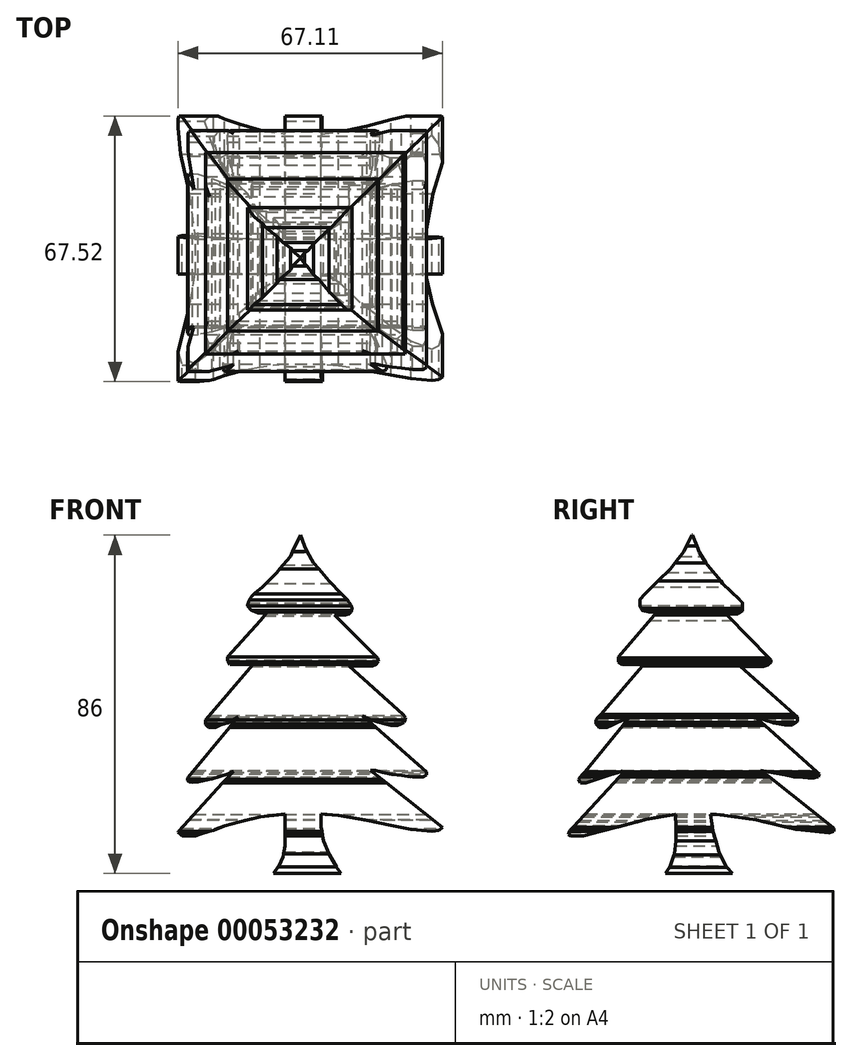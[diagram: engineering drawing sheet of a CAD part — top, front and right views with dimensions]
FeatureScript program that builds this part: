
annotation { "Feature Type Name" : "Feature", "Feature Type Description" : "" }
export const myFeature = defineFeature(function(context is Context, id is Id, definition is map)
    precondition{}
    {
        {
            var Q0;
            Q0=qCreatedBy(makeId("Front.planeOp"),FACE);
            var sketch = newSketch(context, id + "F0", { "sketchPlane" : qUnion([Q0])});
            skLineSegment(sketch, "E0", {"start": v(0, 37.34) * mm, "end": v(-2.57, 31.9) * mm});
            skLineSegment(sketch, "E1", {"start": v(-2.57, 31.9) * mm, "end": v(-6, 27.88) * mm});
            skLineSegment(sketch, "E2", {"start": v(-6, 27.88) * mm, "end": v(-9.62, 24.16) * mm});
            skLineSegment(sketch, "E3", {"start": v(-9.62, 24.16) * mm, "end": v(-13.44, 21.04) * mm});
            skLineSegment(sketch, "E4", {"start": v(-13.44, 21.04) * mm, "end": v(-13.44, 19.43) * mm});
            skLineSegment(sketch, "E5", {"start": v(-13.44, 19.43) * mm, "end": v(-12.53, 18.32) * mm});
            skLineSegment(sketch, "E6", {"start": v(-12.53, 18.32) * mm, "end": v(-10.82, 17.52) * mm});
            skLineSegment(sketch, "E7", {"start": v(-10.82, 17.52) * mm, "end": v(-8.61, 17.52) * mm});
            skLineSegment(sketch, "E8", {"start": v(-8.61, 17.52) * mm, "end": v(-10.12, 15.6) * mm});
            skLineSegment(sketch, "E9", {"start": v(-10.12, 15.6) * mm, "end": v(-18.47, 6.45) * mm});
            skLineSegment(sketch, "E10", {"start": v(-18.47, 6.45) * mm, "end": v(-18.47, 5.32) * mm});
            skLineSegment(sketch, "E11", {"start": v(-18.47, 5.32) * mm, "end": v(-17.83, 4.51) * mm});
            skLineSegment(sketch, "E12", {"start": v(-17.83, 4.51) * mm, "end": v(-16.4, 4.51) * mm});
            skLineSegment(sketch, "E13", {"start": v(-16.4, 4.51) * mm, "end": v(-14.4, 4.51) * mm});
            skLineSegment(sketch, "E14", {"start": v(-14.4, 4.51) * mm, "end": v(-12.08, 4.51) * mm});
            skLineSegment(sketch, "E15", {"start": v(-12.08, 4.51) * mm, "end": v(-24.1, -9.58) * mm});
            skLineSegment(sketch, "E16", {"start": v(-24.1, -9.58) * mm, "end": v(-24.1, -10.69) * mm});
            skLineSegment(sketch, "E17", {"start": v(-24.1, -10.69) * mm, "end": v(-23.3, -11.5) * mm});
            skLineSegment(sketch, "E18", {"start": v(-23.3, -11.5) * mm, "end": v(-21.58, -11.5) * mm});
            skLineSegment(sketch, "E19", {"start": v(-21.58, -11.5) * mm, "end": v(-20.27, -10.92) * mm});
            skLineSegment(sketch, "E20", {"start": v(-20.27, -10.92) * mm, "end": v(-18.56, -10.32) * mm});
            skLineSegment(sketch, "E21", {"start": v(-18.56, -10.32) * mm, "end": v(-15.85, -8.81) * mm});
            skLineSegment(sketch, "E22", {"start": v(-15.85, -8.81) * mm, "end": v(-28.5, -24.2) * mm});
            skLineSegment(sketch, "E23", {"start": v(-22.4, -24.55) * mm, "end": v(-20.48, -23.91) * mm});
            skLineSegment(sketch, "E24", {"start": v(-20.48, -23.91) * mm, "end": v(-18.4, -23.27) * mm});
            skLineSegment(sketch, "E25", {"start": v(-18.4, -23.27) * mm, "end": v(-17.05, -22.63) * mm});
            skLineSegment(sketch, "E26", {"start": v(-17.05, -22.63) * mm, "end": v(-31.07, -38.15) * mm});
            skLineSegment(sketch, "E27", {"start": v(-31.07, -38.15) * mm, "end": v(-30.1, -39.02) * mm});
            skLineSegment(sketch, "E28", {"start": v(-30.1, -39.02) * mm, "end": v(-26.6, -39.02) * mm});
            skLineSegment(sketch, "E29", {"start": v(-26.6, -39.02) * mm, "end": v(-22.1, -37.61) * mm});
            skLineSegment(sketch, "E30", {"start": v(-22.1, -37.61) * mm, "end": v(-19.29, -36.5) * mm});
            skLineSegment(sketch, "E31", {"start": v(-19.29, -36.5) * mm, "end": v(-15.46, -35.5) * mm});
            skLineSegment(sketch, "E32", {"start": v(-15.46, -35.5) * mm, "end": v(-10.23, -34.3) * mm});
            skLineSegment(sketch, "E33", {"start": v(-10.23, -34.3) * mm, "end": v(-2.99, -33.39) * mm});
            skLineSegment(sketch, "E34", {"start": v(-2.99, -33.39) * mm, "end": v(4.36, -33.39) * mm});
            skLineSegment(sketch, "E35", {"start": v(4.36, -33.39) * mm, "end": v(9.69, -33.9) * mm});
            skLineSegment(sketch, "E36", {"start": v(9.69, -33.9) * mm, "end": v(16.95, -35.14) * mm});
            skLineSegment(sketch, "E37", {"start": v(16.95, -35.14) * mm, "end": v(22.98, -36.42) * mm});
            skLineSegment(sketch, "E38", {"start": v(22.98, -36.42) * mm, "end": v(28.05, -37.4) * mm});
            skLineSegment(sketch, "E39", {"start": v(28.05, -37.4) * mm, "end": v(33.37, -37.96) * mm});
            skLineSegment(sketch, "E40", {"start": v(33.37, -37.96) * mm, "end": v(35.23, -37.7) * mm});
            skLineSegment(sketch, "E41", {"start": v(35.23, -37.7) * mm, "end": v(36.04, -36.93) * mm});
            skLineSegment(sketch, "E42", {"start": v(36.04, -36.93) * mm, "end": v(17.8, -22.45) * mm});
            skLineSegment(sketch, "E43", {"start": v(17.8, -22.45) * mm, "end": v(19.05, -22.45) * mm});
            skLineSegment(sketch, "E44", {"start": v(25.64, -23.69) * mm, "end": v(28.4, -24.14) * mm});
            skLineSegment(sketch, "E45", {"start": v(28.4, -24.14) * mm, "end": v(31.12, -24.14) * mm});
            skLineSegment(sketch, "E46", {"start": v(31.12, -24.14) * mm, "end": v(32.03, -23.64) * mm});
            skLineSegment(sketch, "E47", {"start": v(32.03, -23.64) * mm, "end": v(32.03, -22.78) * mm});
            skLineSegment(sketch, "E48", {"start": v(32.03, -22.78) * mm, "end": v(15.82, -8.6) * mm});
            skLineSegment(sketch, "E49", {"start": v(15.82, -8.6) * mm, "end": v(17.66, -9.48) * mm});
            skLineSegment(sketch, "E50", {"start": v(17.66, -9.48) * mm, "end": v(19.62, -10.12) * mm});
            skLineSegment(sketch, "E51", {"start": v(19.62, -10.12) * mm, "end": v(22.97, -11) * mm});
            skLineSegment(sketch, "E52", {"start": v(22.97, -11) * mm, "end": v(24.66, -11) * mm});
            skLineSegment(sketch, "E53", {"start": v(24.66, -11) * mm, "end": v(26.34, -10.3) * mm});
            skLineSegment(sketch, "E54", {"start": v(26.34, -10.3) * mm, "end": v(26.66, -9.02) * mm});
            skLineSegment(sketch, "E55", {"start": v(26.66, -9.02) * mm, "end": v(26, -8.21) * mm});
            skLineSegment(sketch, "E56", {"start": v(26, -8.21) * mm, "end": v(12.31, 4.1) * mm});
            skLineSegment(sketch, "E57", {"start": v(12.31, 4.1) * mm, "end": v(13.45, 4.1) * mm});
            skLineSegment(sketch, "E58", {"start": v(13.45, 4.1) * mm, "end": v(18.29, 4.1) * mm});
            skLineSegment(sketch, "E59", {"start": v(18.29, 4.1) * mm, "end": v(19.2, 4.48) * mm});
            skLineSegment(sketch, "E60", {"start": v(19.2, 4.48) * mm, "end": v(19.84, 5.29) * mm});
            skLineSegment(sketch, "E61", {"start": v(19.84, 5.29) * mm, "end": v(19.53, 6.11) * mm});
            skLineSegment(sketch, "E62", {"start": v(19.53, 6.11) * mm, "end": v(8.62, 17.05) * mm});
            skLineSegment(sketch, "E63", {"start": v(8.62, 17.05) * mm, "end": v(9.68, 17.05) * mm});
            skLineSegment(sketch, "E64", {"start": v(9.68, 17.05) * mm, "end": v(11.49, 17.05) * mm});
            skLineSegment(sketch, "E65", {"start": v(11.49, 17.05) * mm, "end": v(12.37, 17.3) * mm});
            skLineSegment(sketch, "E66", {"start": v(12.37, 17.3) * mm, "end": v(12.9, 17.81) * mm});
            skLineSegment(sketch, "E67", {"start": v(12.9, 17.81) * mm, "end": v(13.1, 18.74) * mm});
            skLineSegment(sketch, "E68", {"start": v(13.1, 18.74) * mm, "end": v(13.1, 19.67) * mm});
            skLineSegment(sketch, "E69", {"start": v(13.1, 19.67) * mm, "end": v(7.2, 25.64) * mm});
            skLineSegment(sketch, "E70", {"start": v(7.2, 25.64) * mm, "end": v(3.3, 30.31) * mm});
            skLineSegment(sketch, "E71", {"start": v(3.3, 30.31) * mm, "end": v(0.97, 34.58) * mm});
            skLineSegment(sketch, "E72", {"start": v(0.97, 34.58) * mm, "end": v(0, 37.34) * mm});
            skLineSegment(sketch, "E73", {"start": v(-3.95, -33.5) * mm, "end": v(-3.95, -41.62) * mm});
            skLineSegment(sketch, "E74", {"start": v(-3.95, -41.62) * mm, "end": v(-4.4, -44.34) * mm});
            skLineSegment(sketch, "E75", {"start": v(-4.4, -44.34) * mm, "end": v(-5.42, -46.69) * mm});
            skLineSegment(sketch, "E76", {"start": v(-5.42, -46.69) * mm, "end": v(-6.8, -48.66) * mm});
            skLineSegment(sketch, "E77", {"start": v(-6.8, -48.66) * mm, "end": v(10.3, -48.66) * mm});
            skLineSegment(sketch, "E78", {"start": v(10.3, -48.66) * mm, "end": v(9.19, -47.12) * mm});
            skLineSegment(sketch, "E79", {"start": v(9.19, -47.12) * mm, "end": v(7.37, -43.86) * mm});
            skLineSegment(sketch, "E80", {"start": v(7.37, -43.86) * mm, "end": v(5.88, -40.3) * mm});
            skLineSegment(sketch, "E81", {"start": v(5.88, -40.3) * mm, "end": v(5.24, -36.78) * mm});
            skLineSegment(sketch, "E82", {"start": v(5.24, -36.78) * mm, "end": v(5.24, -33.47) * mm});
            skLineSegment(sketch, "E83", {"start": v(19.05, -22.45) * mm, "end": v(20.88, -22.89) * mm});
            skLineSegment(sketch, "E84", {"start": v(20.88, -22.89) * mm, "end": v(23.32, -23.43) * mm});
            skLineSegment(sketch, "E85", {"start": v(23.32, -23.43) * mm, "end": v(25.64, -23.69) * mm});
            skLineSegment(sketch, "E86", {"start": v(-28.5, -24.2) * mm, "end": v(-28.74, -24.93) * mm});
            skLineSegment(sketch, "E87", {"start": v(-28.74, -24.93) * mm, "end": v(-28.34, -25.4) * mm});
            skLineSegment(sketch, "E88", {"start": v(-28.34, -25.4) * mm, "end": v(-27.37, -25.52) * mm});
            skLineSegment(sketch, "E89", {"start": v(-27.37, -25.52) * mm, "end": v(-26.06, -25.4) * mm});
            skLineSegment(sketch, "E90", {"start": v(-26.06, -25.4) * mm, "end": v(-22.4, -24.55) * mm});
            skSolve(sketch);
        }
        {
            var Q0;
            Q0=qCreatedBy(makeId("Right.planeOp"),FACE);
            var sketch = newSketch(context, id + "F1", { "sketchPlane" : qUnion([Q0])});
            skLineSegment(sketch, "E91", {"start": v(0, 37.47) * mm, "end": v(1.86, 32.89) * mm});
            skLineSegment(sketch, "E92", {"start": v(1.86, 32.89) * mm, "end": v(3.83, 29.8) * mm});
            skLineSegment(sketch, "E93", {"start": v(3.83, 29.8) * mm, "end": v(7.67, 25.1) * mm});
            skLineSegment(sketch, "E94", {"start": v(7.67, 25.1) * mm, "end": v(12.79, 20.16) * mm});
            skLineSegment(sketch, "E95", {"start": v(12.79, 20.16) * mm, "end": v(12.79, 19.2) * mm});
            skLineSegment(sketch, "E96", {"start": v(12.79, 19.2) * mm, "end": v(12.79, 18.04) * mm});
            skPoint(sketch, "E96.endSnap0", {"position": v(12.79, 19.68) * mm});
            skLineSegment(sketch, "E97", {"start": v(12.79, 18.04) * mm, "end": v(11.59, 17.36) * mm});
            skLineSegment(sketch, "E98", {"start": v(11.59, 17.36) * mm, "end": v(9.03, 17.36) * mm});
            skLineSegment(sketch, "E99", {"start": v(9.03, 17.36) * mm, "end": v(9.03, 16.8) * mm});
            skLineSegment(sketch, "E100", {"start": v(9.03, 16.8) * mm, "end": v(19.98, 5.63) * mm});
            skLineSegment(sketch, "E101", {"start": v(19.98, 5.63) * mm, "end": v(19.98, 4.99) * mm});
            skLineSegment(sketch, "E102", {"start": v(19.98, 4.99) * mm, "end": v(19.16, 4.35) * mm});
            skLineSegment(sketch, "E103", {"start": v(19.16, 4.35) * mm, "end": v(18.06, 3.96) * mm});
            skLineSegment(sketch, "E104", {"start": v(18.06, 3.96) * mm, "end": v(12.19, 3.96) * mm});
            skLineSegment(sketch, "E105", {"start": v(12.19, 3.96) * mm, "end": v(26.75, -8.88) * mm});
            skLineSegment(sketch, "E106", {"start": v(26.75, -8.88) * mm, "end": v(26.75, -10) * mm});
            skLineSegment(sketch, "E107", {"start": v(26.75, -10) * mm, "end": v(25.44, -10.91) * mm});
            skLineSegment(sketch, "E108", {"start": v(25.44, -10.91) * mm, "end": v(24.46, -10.91) * mm});
            skLineSegment(sketch, "E109", {"start": v(24.46, -10.91) * mm, "end": v(23.57, -10.91) * mm});
            skLineSegment(sketch, "E110", {"start": v(23.57, -10.91) * mm, "end": v(20.59, -10.36) * mm});
            skLineSegment(sketch, "E111", {"start": v(20.59, -10.36) * mm, "end": v(18.77, -9.8) * mm});
            skLineSegment(sketch, "E112", {"start": v(18.77, -9.8) * mm, "end": v(15.48, -8.42) * mm});
            skLineSegment(sketch, "E113", {"start": v(15.48, -8.42) * mm, "end": v(32.3, -23.34) * mm});
            skLineSegment(sketch, "E114", {"start": v(32.3, -23.34) * mm, "end": v(32.02, -24.04) * mm});
            skLineSegment(sketch, "E115", {"start": v(32.02, -24.04) * mm, "end": v(30.93, -24.36) * mm});
            skLineSegment(sketch, "E116", {"start": v(30.93, -24.36) * mm, "end": v(29.35, -24.36) * mm});
            skLineSegment(sketch, "E117", {"start": v(29.35, -24.36) * mm, "end": v(25.78, -24.06) * mm});
            skLineSegment(sketch, "E118", {"start": v(25.78, -24.06) * mm, "end": v(17.38, -22.39) * mm});
            skLineSegment(sketch, "E119", {"start": v(17.38, -22.39) * mm, "end": v(36.02, -37.15) * mm});
            skLineSegment(sketch, "E120", {"start": v(36.02, -37.15) * mm, "end": v(36.02, -37.91) * mm});
            skLineSegment(sketch, "E121", {"start": v(36.02, -37.91) * mm, "end": v(34.67, -38.32) * mm});
            skLineSegment(sketch, "E122", {"start": v(34.67, -38.32) * mm, "end": v(26.34, -37.46) * mm});
            skLineSegment(sketch, "E123", {"start": v(26.34, -37.46) * mm, "end": v(16.3, -35.04) * mm});
            skLineSegment(sketch, "E124", {"start": v(16.3, -35.04) * mm, "end": v(6.08, -33.56) * mm});
            skLineSegment(sketch, "E125", {"start": v(6.08, -33.56) * mm, "end": v(-4.22, -33.56) * mm});
            skLineSegment(sketch, "E126", {"start": v(-4.22, -33.56) * mm, "end": v(-11.75, -34.9) * mm});
            skLineSegment(sketch, "E127", {"start": v(-11.75, -34.9) * mm, "end": v(-19.2, -36.88) * mm});
            skLineSegment(sketch, "E128", {"start": v(-19.2, -36.88) * mm, "end": v(-27.62, -39.11) * mm});
            skLineSegment(sketch, "E129", {"start": v(-27.62, -39.11) * mm, "end": v(-30.87, -39.11) * mm});
            skLineSegment(sketch, "E130", {"start": v(-30.87, -39.11) * mm, "end": v(-31.5, -38.7) * mm});
            skLineSegment(sketch, "E131", {"start": v(-31.5, -38.7) * mm, "end": v(-31.25, -37.97) * mm});
            skLineSegment(sketch, "E132", {"start": v(-31.25, -37.97) * mm, "end": v(-17.36, -22.95) * mm});
            skLineSegment(sketch, "E133", {"start": v(-17.36, -22.95) * mm, "end": v(-17.74, -22.6) * mm});
            skLineSegment(sketch, "E134", {"start": v(-17.74, -22.6) * mm, "end": v(-27.05, -25.66) * mm});
            skLineSegment(sketch, "E135", {"start": v(-27.05, -25.66) * mm, "end": v(-28.36, -25.66) * mm});
            skLineSegment(sketch, "E136", {"start": v(-28.36, -25.66) * mm, "end": v(-28.87, -24.73) * mm});
            skLineSegment(sketch, "E137", {"start": v(-28.87, -24.73) * mm, "end": v(-16.1, -9.1) * mm});
            skLineSegment(sketch, "E138", {"start": v(-16.1, -9.1) * mm, "end": v(-17.17, -9.45) * mm});
            skLineSegment(sketch, "E139", {"start": v(-17.17, -9.45) * mm, "end": v(-19.5, -10.52) * mm});
            skLineSegment(sketch, "E140", {"start": v(-19.5, -10.52) * mm, "end": v(-21.74, -11.51) * mm});
            skLineSegment(sketch, "E141", {"start": v(-21.74, -11.51) * mm, "end": v(-23.7, -11.51) * mm});
            skLineSegment(sketch, "E142", {"start": v(-23.7, -11.51) * mm, "end": v(-24.43, -10.61) * mm});
            skLineSegment(sketch, "E143", {"start": v(-24.43, -10.61) * mm, "end": v(-24.43, -9.58) * mm});
            skLineSegment(sketch, "E144", {"start": v(-24.43, -9.58) * mm, "end": v(-12.31, 4.52) * mm});
            skLineSegment(sketch, "E145", {"start": v(-12.31, 4.52) * mm, "end": v(-17.68, 4.52) * mm});
            skLineSegment(sketch, "E146", {"start": v(-17.68, 4.52) * mm, "end": v(-18.7, 5.08) * mm});
            skLineSegment(sketch, "E147", {"start": v(-18.7, 5.08) * mm, "end": v(-18.7, 6.38) * mm});
            skLineSegment(sketch, "E148", {"start": v(-18.7, 6.38) * mm, "end": v(-8.98, 17.79) * mm});
            skLineSegment(sketch, "E149", {"start": v(-8.98, 17.79) * mm, "end": v(-10.96, 17.79) * mm});
            skLineSegment(sketch, "E150", {"start": v(-10.96, 17.79) * mm, "end": v(-12.7, 18.24) * mm});
            skLineSegment(sketch, "E151", {"start": v(-12.7, 18.24) * mm, "end": v(-13.33, 19.37) * mm});
            skLineSegment(sketch, "E152", {"start": v(-13.33, 19.37) * mm, "end": v(-13.33, 20.9) * mm});
            skLineSegment(sketch, "E153", {"start": v(-13.33, 20.9) * mm, "end": v(-11.97, 22.36) * mm});
            skLineSegment(sketch, "E154", {"start": v(-11.97, 22.36) * mm, "end": v(-5.6, 28.68) * mm});
            skLineSegment(sketch, "E155", {"start": v(-5.6, 28.68) * mm, "end": v(-2.15, 33.2) * mm});
            skLineSegment(sketch, "E156", {"start": v(-2.15, 33.2) * mm, "end": v(0, 37.47) * mm});
            skLineSegment(sketch, "E157", {"start": v(4.67, -33.56) * mm, "end": v(5.3, -37.95) * mm});
            skLineSegment(sketch, "E158", {"start": v(5.3, -37.95) * mm, "end": v(6.77, -43.15) * mm});
            skLineSegment(sketch, "E159", {"start": v(6.77, -43.15) * mm, "end": v(8.5, -46.79) * mm});
            skLineSegment(sketch, "E160", {"start": v(8.5, -46.79) * mm, "end": v(10.54, -48.99) * mm});
            skLineSegment(sketch, "E161", {"start": v(10.54, -48.99) * mm, "end": v(-6.97, -48.99) * mm});
            skLineSegment(sketch, "E162", {"start": v(-6.97, -48.99) * mm, "end": v(-5.7, -47) * mm});
            skLineSegment(sketch, "E163", {"start": v(-5.7, -47) * mm, "end": v(-4.52, -43.66) * mm});
            skLineSegment(sketch, "E164", {"start": v(-4.52, -43.66) * mm, "end": v(-4.1, -39.09) * mm});
            skLineSegment(sketch, "E165", {"start": v(-4.1, -39.09) * mm, "end": v(-4.22, -33.56) * mm});
            skSolve(sketch);
        }
        {
            var Q0;
            Q0 = qSketchRegion(id + "F0", true);
            extrude(context, id + "F2", {"entities" : qUnion([Q0]), "depth" : 38.1 * mm, "hasSecondDirection" : true, "secondDirectionOppositeDirection" : true, "secondDirectionDepth" : 38.1 * mm});
        }
        {
            var Q0;
            Q0 = qSketchRegion(id + "F1", true);
            extrude(context, id + "F3", {"entities" : qUnion([Q0]), "operationType" : NewBodyOperationType.INTERSECT, "oppositeDirection" : true, "depth" : 38.1 * mm, "hasSecondDirection" : true, "secondDirectionOppositeDirection" : false, "secondDirectionDepth" : 38.1 * mm});
        }
        {
            var Q0;
            Q0=makeQuery(id+"F3.boolean.opBoolean","INTERSECT",EDGE,{"derivedFrom":[makeQuery(id+"F2.opExtrude","SWEPT_FACE",FACE,{"disambiguationData":[OSD([sQuery(id+"F0.wireOp",EDGE,"E62")])]}),makeQuery(id+"F3.boolean.toolComplement.opBoolean","COPY",FACE,{"derivedFrom":makeQuery(id+"F3.opExtrude","SWEPT_FACE",FACE,{"disambiguationData":[OSD([sQuery(id+"F1.wireOp",EDGE,"E148")])]})})]});
            var Q1;
            Q1=makeQuery(id+"F3.boolean.opBoolean","INTERSECT",EDGE,{"derivedFrom":[makeQuery(id+"F2.opExtrude","SWEPT_FACE",FACE,{"disambiguationData":[OSD([sQuery(id+"F0.wireOp",EDGE,"E62")])]}),makeQuery(id+"F3.boolean.toolComplement.opBoolean","COPY",FACE,{"derivedFrom":makeQuery(id+"F3.opExtrude","SWEPT_FACE",FACE,{"disambiguationData":[OSD([sQuery(id+"F1.wireOp",EDGE,"E100")])]})})]});
            var Q2;
            Q2=makeQuery(id+"F3.boolean.opBoolean","INTERSECT",EDGE,{"derivedFrom":[makeQuery(id+"F2.opExtrude","SWEPT_FACE",FACE,{"disambiguationData":[OSD([sQuery(id+"F0.wireOp",EDGE,"E56")])]}),makeQuery(id+"F3.boolean.toolComplement.opBoolean","COPY",FACE,{"derivedFrom":makeQuery(id+"F3.opExtrude","SWEPT_FACE",FACE,{"disambiguationData":[OSD([sQuery(id+"F1.wireOp",EDGE,"E144")])]})})]});
            var Q3;
            Q3=makeQuery(id+"F3.boolean.opBoolean","INTERSECT",EDGE,{"derivedFrom":[makeQuery(id+"F2.opExtrude","SWEPT_FACE",FACE,{"disambiguationData":[OSD([sQuery(id+"F0.wireOp",EDGE,"E9")])]}),makeQuery(id+"F3.boolean.toolComplement.opBoolean","COPY",FACE,{"derivedFrom":makeQuery(id+"F3.opExtrude","SWEPT_FACE",FACE,{"disambiguationData":[OSD([sQuery(id+"F1.wireOp",EDGE,"E148")])]})})]});
            var Q4;
            Q4=makeQuery(id+"F3.boolean.opBoolean","INTERSECT",EDGE,{"derivedFrom":[makeQuery(id+"F2.opExtrude","SWEPT_FACE",FACE,{"disambiguationData":[OSD([sQuery(id+"F0.wireOp",EDGE,"E9")])]}),makeQuery(id+"F3.boolean.toolComplement.opBoolean","COPY",FACE,{"derivedFrom":makeQuery(id+"F3.opExtrude","SWEPT_FACE",FACE,{"disambiguationData":[OSD([sQuery(id+"F1.wireOp",EDGE,"E100")])]})})]});
            var Q5;
            Q5=makeQuery(id+"F3.boolean.opBoolean","INTERSECT",EDGE,{"derivedFrom":[makeQuery(id+"F2.opExtrude","SWEPT_FACE",FACE,{"disambiguationData":[OSD([sQuery(id+"F0.wireOp",EDGE,"E15")])]}),makeQuery(id+"F3.boolean.toolComplement.opBoolean","COPY",FACE,{"derivedFrom":makeQuery(id+"F3.opExtrude","SWEPT_FACE",FACE,{"disambiguationData":[OSD([sQuery(id+"F1.wireOp",EDGE,"E105")])]})})]});
            var Q6;
            Q6=makeQuery(id+"F3.boolean.opBoolean","INTERSECT",EDGE,{"derivedFrom":[makeQuery(id+"F2.opExtrude","SWEPT_FACE",FACE,{"disambiguationData":[OSD([sQuery(id+"F0.wireOp",EDGE,"E15")])]}),makeQuery(id+"F3.boolean.toolComplement.opBoolean","COPY",FACE,{"derivedFrom":makeQuery(id+"F3.opExtrude","SWEPT_FACE",FACE,{"disambiguationData":[OSD([sQuery(id+"F1.wireOp",EDGE,"E144")])]})})]});
            var Q7;
            Q7=makeQuery(id+"F3.boolean.opBoolean","INTERSECT",EDGE,{"derivedFrom":[makeQuery(id+"F2.opExtrude","SWEPT_FACE",FACE,{"disambiguationData":[OSD([sQuery(id+"F0.wireOp",EDGE,"E56")])]}),makeQuery(id+"F3.boolean.toolComplement.opBoolean","COPY",FACE,{"derivedFrom":makeQuery(id+"F3.opExtrude","SWEPT_FACE",FACE,{"disambiguationData":[OSD([sQuery(id+"F1.wireOp",EDGE,"E105")])]})})]});
            var Q8;
            Q8=makeQuery(id+"F3.boolean.opBoolean","INTERSECT",EDGE,{"derivedFrom":[makeQuery(id+"F2.opExtrude","SWEPT_FACE",FACE,{"disambiguationData":[OSD([sQuery(id+"F0.wireOp",EDGE,"E48")])]}),makeQuery(id+"F3.boolean.toolComplement.opBoolean","COPY",FACE,{"derivedFrom":makeQuery(id+"F3.opExtrude","SWEPT_FACE",FACE,{"disambiguationData":[OSD([sQuery(id+"F1.wireOp",EDGE,"E113")])]})})]});
            var Q9;
            Q9=makeQuery(id+"F3.boolean.opBoolean","INTERSECT",EDGE,{"derivedFrom":[makeQuery(id+"F2.opExtrude","SWEPT_FACE",FACE,{"disambiguationData":[OSD([sQuery(id+"F0.wireOp",EDGE,"E42")])]}),makeQuery(id+"F3.boolean.toolComplement.opBoolean","COPY",FACE,{"derivedFrom":makeQuery(id+"F3.opExtrude","SWEPT_FACE",FACE,{"disambiguationData":[OSD([sQuery(id+"F1.wireOp",EDGE,"E119")])]})})]});
            var Q10;
            Q10=makeQuery(id+"F3.boolean.opBoolean","INTERSECT",EDGE,{"derivedFrom":[makeQuery(id+"F2.opExtrude","SWEPT_FACE",FACE,{"disambiguationData":[OSD([sQuery(id+"F0.wireOp",EDGE,"E26")])]}),makeQuery(id+"F3.boolean.toolComplement.opBoolean","COPY",FACE,{"derivedFrom":makeQuery(id+"F3.opExtrude","SWEPT_FACE",FACE,{"disambiguationData":[OSD([sQuery(id+"F1.wireOp",EDGE,"E119")])]})})]});
            var Q11;
            Q11=makeQuery(id+"F3.boolean.opBoolean","INTERSECT",EDGE,{"derivedFrom":[makeQuery(id+"F2.opExtrude","SWEPT_FACE",FACE,{"disambiguationData":[OSD([sQuery(id+"F0.wireOp",EDGE,"E22")])]}),makeQuery(id+"F3.boolean.toolComplement.opBoolean","COPY",FACE,{"derivedFrom":makeQuery(id+"F3.opExtrude","SWEPT_FACE",FACE,{"disambiguationData":[OSD([sQuery(id+"F1.wireOp",EDGE,"E113")])]})})]});
            var Q12;
            Q12=makeQuery(id+"F3.boolean.opBoolean","INTERSECT",EDGE,{"derivedFrom":[makeQuery(id+"F2.opExtrude","SWEPT_FACE",FACE,{"disambiguationData":[OSD([sQuery(id+"F0.wireOp",EDGE,"E26")])]}),makeQuery(id+"F3.boolean.toolComplement.opBoolean","COPY",FACE,{"derivedFrom":makeQuery(id+"F3.opExtrude","SWEPT_FACE",FACE,{"disambiguationData":[OSD([sQuery(id+"F1.wireOp",EDGE,"E132")])]})})]});
            var Q13;
            Q13=makeQuery(id+"F3.boolean.opBoolean","INTERSECT",EDGE,{"derivedFrom":[makeQuery(id+"F2.opExtrude","SWEPT_FACE",FACE,{"disambiguationData":[OSD([sQuery(id+"F0.wireOp",EDGE,"E22")])]}),makeQuery(id+"F3.boolean.toolComplement.opBoolean","COPY",FACE,{"derivedFrom":makeQuery(id+"F3.opExtrude","SWEPT_FACE",FACE,{"disambiguationData":[OSD([sQuery(id+"F1.wireOp",EDGE,"E137")])]})})]});
            var Q14;
            Q14=makeQuery(id+"F3.boolean.opBoolean","INTERSECT",EDGE,{"derivedFrom":[makeQuery(id+"F2.opExtrude","SWEPT_FACE",FACE,{"disambiguationData":[OSD([sQuery(id+"F0.wireOp",EDGE,"E48")])]}),makeQuery(id+"F3.boolean.toolComplement.opBoolean","COPY",FACE,{"derivedFrom":makeQuery(id+"F3.opExtrude","SWEPT_FACE",FACE,{"disambiguationData":[OSD([sQuery(id+"F1.wireOp",EDGE,"E137")])]})})]});
            var Q15;
            Q15=makeQuery(id+"F3.boolean.opBoolean","INTERSECT",EDGE,{"derivedFrom":[makeQuery(id+"F2.opExtrude","SWEPT_FACE",FACE,{"disambiguationData":[OSD([sQuery(id+"F0.wireOp",EDGE,"E42")])]}),makeQuery(id+"F3.boolean.toolComplement.opBoolean","COPY",FACE,{"derivedFrom":makeQuery(id+"F3.opExtrude","SWEPT_FACE",FACE,{"disambiguationData":[OSD([sQuery(id+"F1.wireOp",EDGE,"E132")])]})})]});
            var Q16;
            Q16=makeQuery(id+"F3.boolean.opBoolean","COPY",EDGE,{"derivedFrom":makeQuery(id+"F3.boolean.toolComplement.opBoolean","COPY",EDGE,{"derivedFrom":makeQuery(id+"F3.opExtrude","SWEPT_EDGE",EDGE,{"disambiguationData":[OSD([sQuery(id+"F1.wireOp",EDGE,"E151"),sQuery(id+"F1.wireOp",EDGE,"E152")])]})})});
            var Q17;
            Q17=makeQuery(id+"F2.opExtrude","SWEPT_EDGE",EDGE,{"disambiguationData":[OSD([sQuery(id+"F0.wireOp",EDGE,"E3"),sQuery(id+"F0.wireOp",EDGE,"E4")])]});
            var Q18;
            Q18=makeQuery(id+"F3.boolean.opBoolean","COPY",EDGE,{"derivedFrom":makeQuery(id+"F3.boolean.toolComplement.opBoolean","COPY",EDGE,{"derivedFrom":makeQuery(id+"F3.opExtrude","SWEPT_EDGE",EDGE,{"disambiguationData":[OSD([sQuery(id+"F1.wireOp",EDGE,"E94"),sQuery(id+"F1.wireOp",EDGE,"E95")])]})})});
            var Q19;
            Q19=makeQuery(id+"F2.opExtrude","SWEPT_EDGE",EDGE,{"disambiguationData":[OSD([sQuery(id+"F0.wireOp",EDGE,"E68"),sQuery(id+"F0.wireOp",EDGE,"E69")])]});
            fillet(context, id + "F4", {"entities" : qUnion([Q0, Q1, Q2, Q3, Q4, Q5, Q6, Q7, Q8, Q9, Q10, Q11, Q12, Q13, Q14, Q15, Q16, Q17, Q18, Q19]), "radius" : 5.08 * mm, "tangentPropagation" : true, "allowEdgeOverflow" : false});
        }
    });
